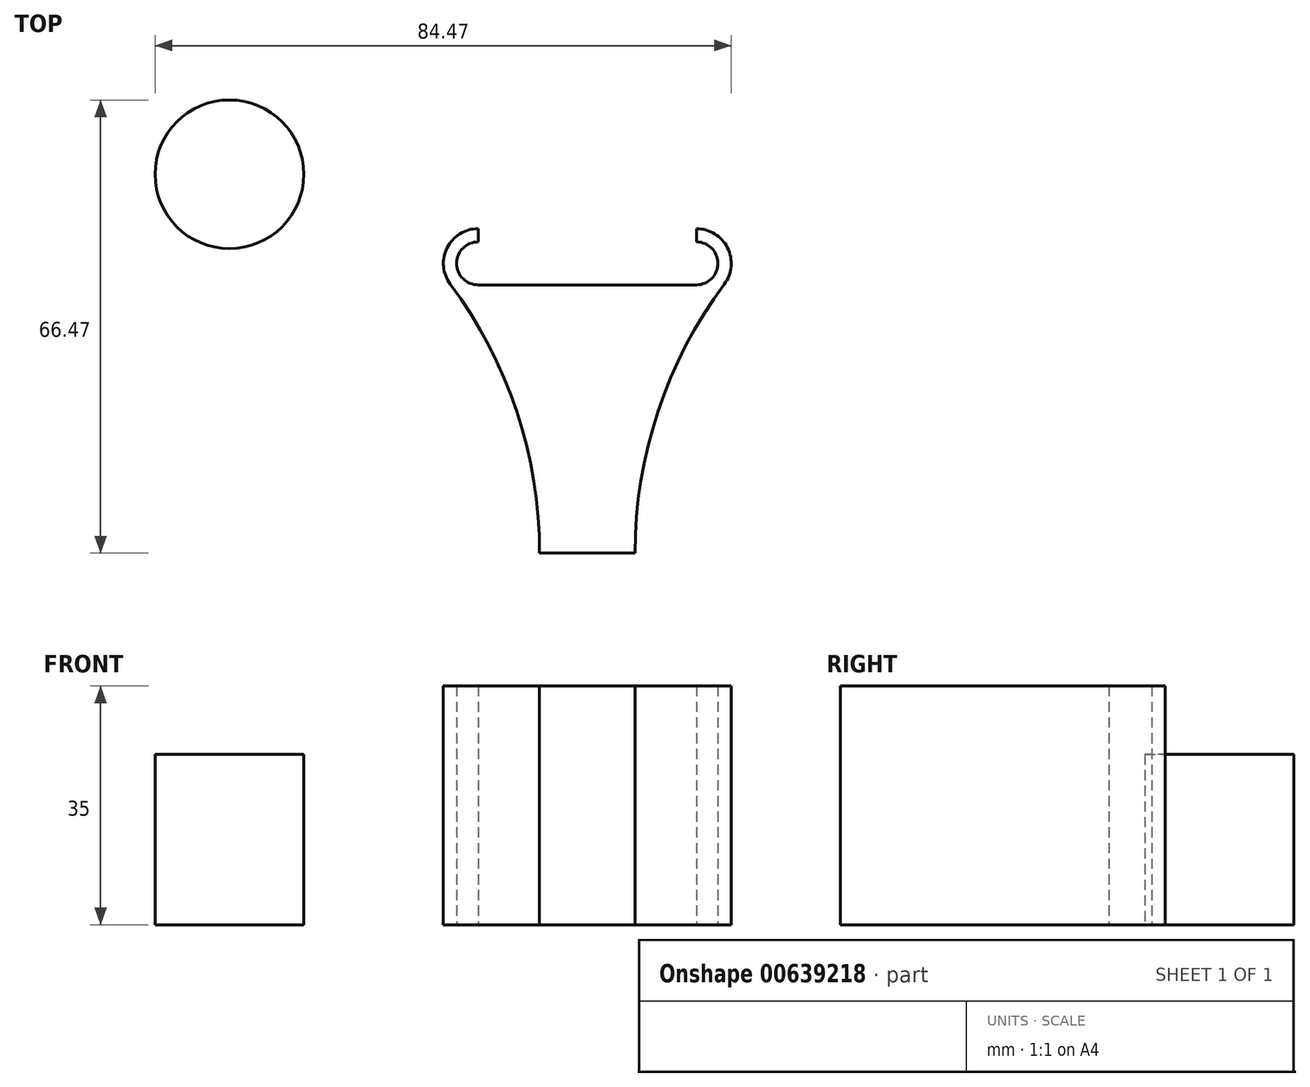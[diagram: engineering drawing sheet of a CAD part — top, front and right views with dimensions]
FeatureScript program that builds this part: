
annotation { "Feature Type Name" : "Feature", "Feature Type Description" : "" }
export const myFeature = defineFeature(function(context is Context, id is Id, definition is map)
    precondition{}
    {
        {
            var Q0;
            Q0=qCreatedBy(makeId("Top.planeOp"),FACE);
            var sketch = newSketch(context, id + "F0", { "sketchPlane" : qUnion([Q0])});
            skLineSegment(sketch, "E0", {"start": v(0, -17.43) * mm, "end": v(-7, -17.43) * mm});
            skLineSegment(sketch, "E1", {"start": v(0, -17.43) * mm, "end": v(7, -17.43) * mm});
            skArc(sketch, "E2", {"start": v(-7, -17.43) * mm, "mid": v(-10.36, 3.36) * mm, "end": v(-20.1, 22.03) * mm});
            skArc(sketch, "E3", {"start": v(20.1, 22.02) * mm, "mid": v(10.36, 3.35) * mm, "end": v(7, -17.43) * mm});
            skPoint(sketch, "E4.start.orphan", {"position": v(-9.34, 0) * mm});
            skArc(sketch, "E5", {"start": v(-16, 30.17) * mm, "mid": v(-20.6, 22.85) * mm, "end": v(-12, 21.92) * mm});
            skArc(sketch, "E6", {"start": v(12, 21.92) * mm, "mid": v(20.59, 22.84) * mm, "end": v(16, 30.17) * mm});
            skLineSegment(sketch, "E7", {"start": v(-16, 28.22) * mm, "end": v(-16, 30.17) * mm});
            skLineSegment(sketch, "E8", {"start": v(16, 28.22) * mm, "end": v(16, 30.17) * mm});
            skArc(sketch, "E9", {"start": v(-16, 28.22) * mm, "mid": v(-19.16, 25.07) * mm, "end": v(-16, 21.92) * mm});
            skArc(sketch, "E10", {"start": v(16, 21.92) * mm, "mid": v(19.15, 25.07) * mm, "end": v(16, 28.22) * mm});
            skLineSegment(sketch, "E11", {"start": v(16, 21.92) * mm, "end": v(-16, 21.92) * mm});
            skSolve(sketch);
        }
        {
            var Q0;
            Q0 = qSketchRegion(id + "F0", true);
            extrude(context, id + "F1", {"entities" : qUnion([Q0]), "depth" : 35 * mm, "offsetDistance" : 25 * mm});
        }
        {
            var Q0;
            Q0=qCreatedBy(makeId("Top.planeOp"),FACE);
            var sketch = newSketch(context, id + "F2", { "sketchPlane" : qUnion([Q0])});
            skCircle(sketch, "E12", {"center": v(-52.47, 38.14) * mm, "radius": 10.9 * mm});
            skSolve(sketch);
        }
        {
            var Q0;
            Q0 = qSketchRegion(id + "F2", true);
            extrude(context, id + "F3", {"entities" : qUnion([Q0]), "depth" : 25 * mm, "offsetDistance" : 25 * mm});
        }
    });
